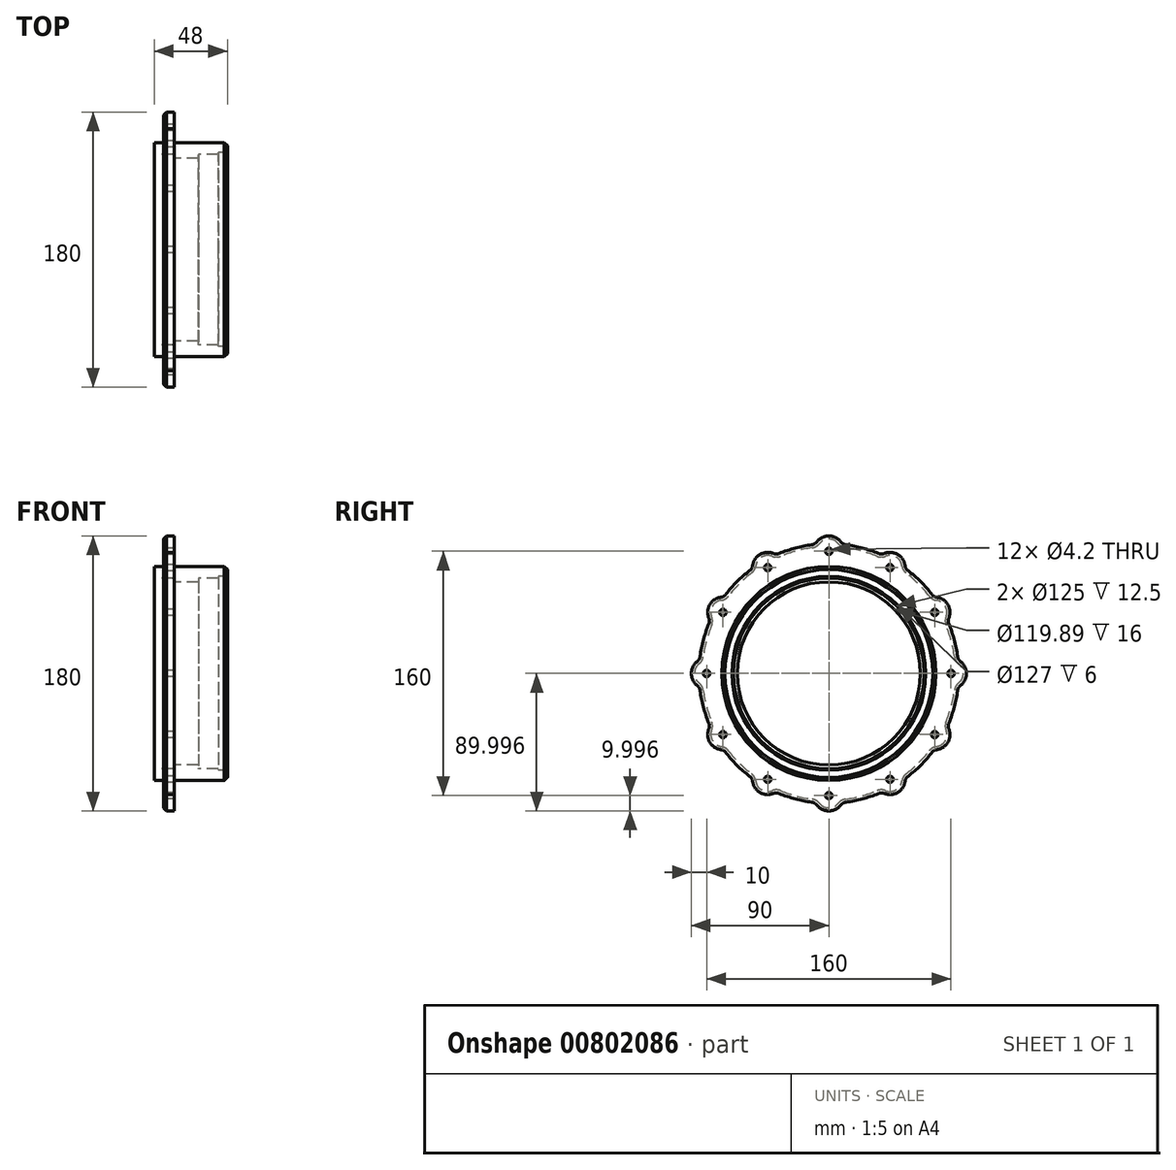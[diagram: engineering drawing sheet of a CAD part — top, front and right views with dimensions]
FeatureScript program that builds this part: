
annotation { "Feature Type Name" : "Feature", "Feature Type Description" : "" }
export const myFeature = defineFeature(function(context is Context, id is Id, definition is map)
    precondition{}
    {
        {
            var Q0;
            Q0=qCreatedBy(makeId("Front.planeOp"),FACE);
            var sketch = newSketch(context, id + "F0", { "sketchPlane" : qUnion([Q0])});
            skLineSegment(sketch, "E0", {"start": v(-16.87, 26.2) * mm, "end": v(-9.87, 26.2) * mm});
            skLineSegment(sketch, "E1", {"start": v(-9.87, 26.2) * mm, "end": v(-9.87, 6.2) * mm});
            skLineSegment(sketch, "E2", {"start": v(-16.87, 26.2) * mm, "end": v(-16.87, 6.2) * mm});
            skLineSegment(sketch, "E3", {"start": v(-16.87, 6.2) * mm, "end": v(-22.87, 6.2) * mm});
            skLineSegment(sketch, "E4", {"start": v(-22.87, 6.2) * mm, "end": v(-22.87, -1.3) * mm});
            skLineSegment(sketch, "E5", {"start": v(-22.87, -1.3) * mm, "end": v(-9.87, -1.3) * mm});
            skLineSegment(sketch, "E6", {"start": v(-9.87, -1.3) * mm, "end": v(-9.87, -3.85) * mm});
            skLineSegment(sketch, "E7", {"start": v(-9.87, -3.85) * mm, "end": v(6.13, -3.85) * mm});
            skLineSegment(sketch, "E8", {"start": v(6.13, -3.85) * mm, "end": v(6.13, -1.3) * mm});
            skLineSegment(sketch, "E9", {"start": v(6.13, -1.3) * mm, "end": v(19.13, -1.3) * mm});
            skLineSegment(sketch, "E10", {"start": v(-16.87, -63.8) * mm, "end": v(53.32, -63.8) * mm, "construction": true});
            skLineSegment(sketch, "E11", {"start": v(19.13, -1.3) * mm, "end": v(19.13, -0.3) * mm});
            skLineSegment(sketch, "E12", {"start": v(19.13, -0.3) * mm, "end": v(25.13, -0.3) * mm});
            skLineSegment(sketch, "E13", {"start": v(-9.87, 6.2) * mm, "end": v(25.13, 6.2) * mm});
            skLineSegment(sketch, "E14", {"start": v(25.13, 6.2) * mm, "end": v(25.13, -0.3) * mm});
            skSolve(sketch);
        }
        {
            var Q0;
            Q0 = qSketchRegion(id + "F0", true);
            var Q1;
            Q1=sQuery(id+"F0.wireOp",EDGE,"E10");
            revolve(context, id + "F1", {"entities" : qUnion([Q0]), "axis" : qUnion([Q1]), "revolveType" : RevolveType.FULL});
        }
        {
            var Q0;
            Q0=makeQuery(id+"F1.opRevolve","SWEPT_FACE",FACE,{"disambiguationData":[OSD([sQuery(id+"F0.wireOp",EDGE,"E2")])]});
            var sketch = newSketch(context, id + "F2", { "sketchPlane" : qUnion([Q0])});
            skLineSegment(sketch, "E15", {"start": v(0, -63.8) * mm, "end": v(0, 16.2) * mm, "construction": true});
            skPoint(sketch, "E16", {"position": v(0, 16.2) * mm});
            skPoint(sketch, "E17.1.0", {"position": v(-40, 5.49) * mm});
            skPoint(sketch, "E17.2.0", {"position": v(-69.28, -23.8) * mm});
            skPoint(sketch, "E17.3.0", {"position": v(-80, -63.8) * mm});
            skPoint(sketch, "E17.4.0", {"position": v(-69.28, -103.8) * mm});
            skPoint(sketch, "E17.5.0", {"position": v(-40, -133.08) * mm});
            skPoint(sketch, "E17.6.0", {"position": v(0, -143.8) * mm});
            skPoint(sketch, "E17.7.0", {"position": v(40, -133.08) * mm});
            skPoint(sketch, "E17.8.0", {"position": v(69.28, -103.8) * mm});
            skPoint(sketch, "E17.9.0", {"position": v(80, -63.8) * mm});
            skPoint(sketch, "E17.10.0", {"position": v(69.28, -23.8) * mm});
            skPoint(sketch, "E17.11.0", {"position": v(40, 5.49) * mm});
            skPoint(sketch, "E17.center", {"position": v(0, -63.8) * mm});
            skSolve(sketch);
        }
        {
            var Q0;
            Q0=sQuery(id+"F2.wireOp",VERTEX,"E16");
            var Q1;
            Q1=sQuery(id+"F2.wireOp",VERTEX,"E17.11.0");
            var Q2;
            Q2=sQuery(id+"F2.wireOp",VERTEX,"E17.10.0");
            var Q3;
            Q3=sQuery(id+"F2.wireOp",VERTEX,"E17.9.0");
            var Q4;
            Q4=sQuery(id+"F2.wireOp",VERTEX,"E17.8.0");
            var Q5;
            Q5=sQuery(id+"F2.wireOp",VERTEX,"E17.7.0");
            var Q6;
            Q6=sQuery(id+"F2.wireOp",VERTEX,"E17.6.0");
            var Q7;
            Q7=sQuery(id+"F2.wireOp",VERTEX,"E17.5.0");
            var Q8;
            Q8=sQuery(id+"F2.wireOp",VERTEX,"E17.4.0");
            var Q9;
            Q9=sQuery(id+"F2.wireOp",VERTEX,"E17.3.0");
            var Q10;
            Q10=sQuery(id+"F2.wireOp",VERTEX,"E17.2.0");
            var Q11;
            Q11=sQuery(id+"F2.wireOp",VERTEX,"E17.1.0");
            var Q12;
            Q12=makeQuery(id+"F1.opRevolve","SWEPT_BODY",BODY,{"disambiguationData":[OSD([sQuery(id+"F0.wireOp",EDGE,"E0"),sQuery(id+"F0.wireOp",EDGE,"E1"),sQuery(id+"F0.wireOp",EDGE,"E2"),sQuery(id+"F0.wireOp",EDGE,"E3"),sQuery(id+"F0.wireOp",EDGE,"E4"),sQuery(id+"F0.wireOp",EDGE,"E5"),sQuery(id+"F0.wireOp",EDGE,"E6"),sQuery(id+"F0.wireOp",EDGE,"E7"),sQuery(id+"F0.wireOp",EDGE,"E8"),sQuery(id+"F0.wireOp",EDGE,"E9"),sQuery(id+"F0.wireOp",EDGE,"E11"),sQuery(id+"F0.wireOp",EDGE,"E12"),sQuery(id+"F0.wireOp",EDGE,"E13"),sQuery(id+"F0.wireOp",EDGE,"E14")])]});
            hole(context, id + "F3", {"style" : HoleStyle.SIMPLE, "endStyle" : HoleEndStyle.THROUGH, "standardTappedOrClearance" : lookupTablePath({ "standard" : "ISO", "engagement" : "75%", "pitch" : "0.8 mm", "size" : "M5", "type" : "Tapped" }), "standardBlindInLast" : lookupTablePath({ "standard" : "ISO", "engagement" : "75%", "pitch" : "0.8 mm", "size" : "M5", "type" : "Tapped" }), "holeDiameter" : 4.2 * mm, "showTappedDepth" : true, "isTappedThrough" : true, "tappedDepth" : 16.82 * mm, "tapClearance" : 3, "startFromSketch" : true, "locations" : qUnion([Q0, Q1, Q2, Q3, Q4, Q5, Q6, Q7, Q8, Q9, Q10, Q11]), "scope" : qUnion([Q12]), "majorDiameter" : 5 * mm});
        }
        {
            var Q0;
            Q0=makeQuery(id+"F1.opRevolve","SWEPT_FACE",FACE,{"disambiguationData":[OSD([sQuery(id+"F0.wireOp",EDGE,"E1")])]});
            var sketch = newSketch(context, id + "F4", { "sketchPlane" : qUnion([Q0])});
            skArc(sketch, "E18", {"start": v(45, 14.15) * mm, "mid": v(40.7, 15.46) * mm, "end": v(36.24, 14.75) * mm});
            skArc(sketch, "E19", {"start": v(7.89, 22.35) * mm, "mid": v(4.39, 25.2) * mm, "end": v(0, 26.2) * mm});
            skArc(sketch, "E20", {"start": v(32.45, 14.77) * mm, "mid": v(22, 18.3) * mm, "end": v(11.18, 20.47) * mm});
            skLineSegment(sketch, "E21", {"start": v(0, -63.8) * mm, "end": v(0, 34.34) * mm, "construction": true});
            skLineSegment(sketch, "E22", {"start": v(0, -63.8) * mm, "end": v(49.04, 21.14) * mm, "construction": true});
            skPoint(sketch, "E23.visualSharp", {"position": v(8.91, 20.74) * mm});
            skArc(sketch, "E23.filletArc", {"start": v(7.89, 22.35) * mm, "mid": v(9.35, 21.09) * mm, "end": v(11.18, 20.47) * mm});
            skPoint(sketch, "E24.visualSharp", {"position": v(34.55, 13.87) * mm});
            skArc(sketch, "E24.filletArc", {"start": v(32.45, 14.77) * mm, "mid": v(34.35, 14.39) * mm, "end": v(36.24, 14.75) * mm});
            skPoint(sketch, "E25.1.0", {"position": v(-34.55, 13.87) * mm});
            skArc(sketch, "E25.1.1", {"start": v(-11.18, 20.47) * mm, "mid": v(-22, 18.3) * mm, "end": v(-32.45, 14.77) * mm});
            skArc(sketch, "E25.1.2", {"start": v(-36.24, 14.75) * mm, "mid": v(-40.7, 15.46) * mm, "end": v(-45, 14.15) * mm});
            skPoint(sketch, "E25.1.3", {"position": v(-8.91, 20.74) * mm});
            skArc(sketch, "E25.1.4", {"start": v(0, 26.2) * mm, "mid": v(-4.39, 25.2) * mm, "end": v(-7.89, 22.35) * mm});
            skArc(sketch, "E25.1.5", {"start": v(-11.18, 20.47) * mm, "mid": v(-9.35, 21.09) * mm, "end": v(-7.89, 22.35) * mm});
            skArc(sketch, "E25.1.6", {"start": v(-36.24, 14.75) * mm, "mid": v(-34.35, 14.39) * mm, "end": v(-32.45, 14.77) * mm});
            skPoint(sketch, "E25.2.0", {"position": v(-68.75, -13.8) * mm});
            skArc(sketch, "E25.2.1", {"start": v(-51.8, 3.6) * mm, "mid": v(-60.1, -3.7) * mm, "end": v(-67.39, -11.98) * mm});
            skArc(sketch, "E25.2.2", {"start": v(-70.66, -13.89) * mm, "mid": v(-74.87, -15.5) * mm, "end": v(-77.94, -18.8) * mm});
            skPoint(sketch, "E25.2.3", {"position": v(-49.99, 4.95) * mm});
            skArc(sketch, "E25.2.4", {"start": v(-45, 14.15) * mm, "mid": v(-48.3, 11.07) * mm, "end": v(-49.9, 6.87) * mm});
            skArc(sketch, "E25.2.5", {"start": v(-51.8, 3.6) * mm, "mid": v(-50.53, 5.04) * mm, "end": v(-49.9, 6.87) * mm});
            skArc(sketch, "E25.2.6", {"start": v(-70.66, -13.89) * mm, "mid": v(-68.84, -13.26) * mm, "end": v(-67.39, -11.98) * mm});
            skPoint(sketch, "E25.3.0", {"position": v(-84.53, -54.88) * mm});
            skArc(sketch, "E25.3.1", {"start": v(-78.56, -31.34) * mm, "mid": v(-82.1, -41.8) * mm, "end": v(-84.26, -52.62) * mm});
            skArc(sketch, "E25.3.2", {"start": v(-86.15, -55.9) * mm, "mid": v(-88.98, -59.4) * mm, "end": v(-90, -63.8) * mm});
            skPoint(sketch, "E25.3.3", {"position": v(-77.66, -29.25) * mm});
            skArc(sketch, "E25.3.4", {"start": v(-77.94, -18.8) * mm, "mid": v(-79.26, -23.1) * mm, "end": v(-78.55, -27.55) * mm});
            skArc(sketch, "E25.3.5", {"start": v(-78.56, -31.34) * mm, "mid": v(-78.18, -29.45) * mm, "end": v(-78.55, -27.55) * mm});
            skArc(sketch, "E25.3.6", {"start": v(-86.15, -55.9) * mm, "mid": v(-84.88, -54.45) * mm, "end": v(-84.26, -52.62) * mm});
            skPoint(sketch, "E25.4.0", {"position": v(-77.66, -98.34) * mm});
            skArc(sketch, "E25.4.1", {"start": v(-84.26, -74.97) * mm, "mid": v(-82.1, -85.8) * mm, "end": v(-78.56, -96.25) * mm});
            skArc(sketch, "E25.4.2", {"start": v(-78.55, -100.04) * mm, "mid": v(-79.26, -104.48) * mm, "end": v(-77.94, -108.8) * mm});
            skPoint(sketch, "E25.4.3", {"position": v(-84.53, -72.7) * mm});
            skArc(sketch, "E25.4.4", {"start": v(-90, -63.8) * mm, "mid": v(-88.98, -68.18) * mm, "end": v(-86.15, -71.68) * mm});
            skArc(sketch, "E25.4.5", {"start": v(-84.26, -74.97) * mm, "mid": v(-84.88, -73.14) * mm, "end": v(-86.15, -71.68) * mm});
            skArc(sketch, "E25.4.6", {"start": v(-78.55, -100.04) * mm, "mid": v(-78.18, -98.14) * mm, "end": v(-78.56, -96.25) * mm});
            skPoint(sketch, "E25.5.0", {"position": v(-49.99, -132.54) * mm});
            skArc(sketch, "E25.5.1", {"start": v(-67.39, -115.6) * mm, "mid": v(-60.1, -123.9) * mm, "end": v(-51.8, -131.18) * mm});
            skArc(sketch, "E25.5.2", {"start": v(-49.9, -134.45) * mm, "mid": v(-48.3, -138.66) * mm, "end": v(-45, -141.74) * mm});
            skPoint(sketch, "E25.5.3", {"position": v(-68.75, -113.78) * mm});
            skArc(sketch, "E25.5.4", {"start": v(-77.94, -108.8) * mm, "mid": v(-74.87, -112.09) * mm, "end": v(-70.66, -113.7) * mm});
            skArc(sketch, "E25.5.5", {"start": v(-67.39, -115.6) * mm, "mid": v(-68.84, -114.33) * mm, "end": v(-70.66, -113.7) * mm});
            skArc(sketch, "E25.5.6", {"start": v(-49.9, -134.45) * mm, "mid": v(-50.53, -132.63) * mm, "end": v(-51.8, -131.18) * mm});
            skPoint(sketch, "E25.6.0", {"position": v(-8.91, -148.33) * mm});
            skArc(sketch, "E25.6.1", {"start": v(-32.45, -142.36) * mm, "mid": v(-22, -145.9) * mm, "end": v(-11.18, -148.06) * mm});
            skArc(sketch, "E25.6.2", {"start": v(-7.89, -149.94) * mm, "mid": v(-4.39, -152.78) * mm, "end": v(0, -153.8) * mm});
            skPoint(sketch, "E25.6.3", {"position": v(-34.55, -141.46) * mm});
            skArc(sketch, "E25.6.4", {"start": v(-45, -141.74) * mm, "mid": v(-40.7, -143.05) * mm, "end": v(-36.24, -142.34) * mm});
            skArc(sketch, "E25.6.5", {"start": v(-32.45, -142.36) * mm, "mid": v(-34.35, -141.98) * mm, "end": v(-36.24, -142.34) * mm});
            skArc(sketch, "E25.6.6", {"start": v(-7.89, -149.94) * mm, "mid": v(-9.35, -148.67) * mm, "end": v(-11.18, -148.06) * mm});
            skPoint(sketch, "E25.7.0", {"position": v(34.55, -141.46) * mm});
            skArc(sketch, "E25.7.1", {"start": v(11.18, -148.06) * mm, "mid": v(22, -145.9) * mm, "end": v(32.45, -142.36) * mm});
            skArc(sketch, "E25.7.2", {"start": v(36.24, -142.34) * mm, "mid": v(40.7, -143.05) * mm, "end": v(45, -141.74) * mm});
            skPoint(sketch, "E25.7.3", {"position": v(8.91, -148.33) * mm});
            skArc(sketch, "E25.7.4", {"start": v(0, -153.8) * mm, "mid": v(4.39, -152.78) * mm, "end": v(7.89, -149.94) * mm});
            skArc(sketch, "E25.7.5", {"start": v(11.18, -148.06) * mm, "mid": v(9.35, -148.67) * mm, "end": v(7.89, -149.94) * mm});
            skArc(sketch, "E25.7.6", {"start": v(36.24, -142.34) * mm, "mid": v(34.35, -141.98) * mm, "end": v(32.45, -142.36) * mm});
            skPoint(sketch, "E25.8.0", {"position": v(68.75, -113.78) * mm});
            skArc(sketch, "E25.8.1", {"start": v(51.8, -131.18) * mm, "mid": v(60.1, -123.9) * mm, "end": v(67.39, -115.6) * mm});
            skArc(sketch, "E25.8.2", {"start": v(70.66, -113.7) * mm, "mid": v(74.87, -112.09) * mm, "end": v(77.94, -108.8) * mm});
            skPoint(sketch, "E25.8.3", {"position": v(49.99, -132.54) * mm});
            skArc(sketch, "E25.8.4", {"start": v(45, -141.74) * mm, "mid": v(48.3, -138.66) * mm, "end": v(49.9, -134.45) * mm});
            skArc(sketch, "E25.8.5", {"start": v(51.8, -131.18) * mm, "mid": v(50.53, -132.63) * mm, "end": v(49.9, -134.45) * mm});
            skArc(sketch, "E25.8.6", {"start": v(70.66, -113.7) * mm, "mid": v(68.84, -114.33) * mm, "end": v(67.39, -115.6) * mm});
            skPoint(sketch, "E25.9.0", {"position": v(84.53, -72.7) * mm});
            skArc(sketch, "E25.9.1", {"start": v(78.56, -96.25) * mm, "mid": v(82.1, -85.8) * mm, "end": v(84.26, -74.97) * mm});
            skArc(sketch, "E25.9.2", {"start": v(86.15, -71.68) * mm, "mid": v(88.98, -68.18) * mm, "end": v(90, -63.8) * mm});
            skPoint(sketch, "E25.9.3", {"position": v(77.66, -98.34) * mm});
            skArc(sketch, "E25.9.4", {"start": v(77.94, -108.8) * mm, "mid": v(79.26, -104.48) * mm, "end": v(78.55, -100.04) * mm});
            skArc(sketch, "E25.9.5", {"start": v(78.56, -96.25) * mm, "mid": v(78.18, -98.14) * mm, "end": v(78.55, -100.04) * mm});
            skArc(sketch, "E25.9.6", {"start": v(86.15, -71.68) * mm, "mid": v(84.88, -73.14) * mm, "end": v(84.26, -74.97) * mm});
            skPoint(sketch, "E25.10.0", {"position": v(77.66, -29.25) * mm});
            skArc(sketch, "E25.10.1", {"start": v(84.26, -52.62) * mm, "mid": v(82.1, -41.8) * mm, "end": v(78.56, -31.34) * mm});
            skArc(sketch, "E25.10.2", {"start": v(78.55, -27.55) * mm, "mid": v(79.26, -23.1) * mm, "end": v(77.94, -18.8) * mm});
            skPoint(sketch, "E25.10.3", {"position": v(84.53, -54.88) * mm});
            skArc(sketch, "E25.10.4", {"start": v(90, -63.8) * mm, "mid": v(88.98, -59.4) * mm, "end": v(86.15, -55.9) * mm});
            skArc(sketch, "E25.10.5", {"start": v(84.26, -52.62) * mm, "mid": v(84.88, -54.45) * mm, "end": v(86.15, -55.9) * mm});
            skArc(sketch, "E25.10.6", {"start": v(78.55, -27.55) * mm, "mid": v(78.18, -29.45) * mm, "end": v(78.56, -31.34) * mm});
            skPoint(sketch, "E25.11.0", {"position": v(49.99, 4.95) * mm});
            skArc(sketch, "E25.11.1", {"start": v(67.39, -11.98) * mm, "mid": v(60.1, -3.7) * mm, "end": v(51.8, 3.6) * mm});
            skArc(sketch, "E25.11.2", {"start": v(49.9, 6.87) * mm, "mid": v(48.3, 11.07) * mm, "end": v(45, 14.15) * mm});
            skPoint(sketch, "E25.11.3", {"position": v(68.75, -13.8) * mm});
            skArc(sketch, "E25.11.4", {"start": v(77.94, -18.8) * mm, "mid": v(74.87, -15.5) * mm, "end": v(70.66, -13.89) * mm});
            skArc(sketch, "E25.11.5", {"start": v(67.39, -11.98) * mm, "mid": v(68.84, -13.26) * mm, "end": v(70.66, -13.89) * mm});
            skArc(sketch, "E25.11.6", {"start": v(49.9, 6.87) * mm, "mid": v(50.53, 5.04) * mm, "end": v(51.8, 3.6) * mm});
            skCircle(sketch, "E26", {"center": v(0, -63.8) * mm, "radius": 105.65 * mm});
            skSolve(sketch);
        }
        {
            var Q0;
            Q0 = qSketchRegion(id + "F4", true);
            extrude(context, id + "F5", {"entities" : qUnion([Q0]), "operationType" : NewBodyOperationType.REMOVE, "endBound" : BoundingType.THROUGH_ALL, "oppositeDirection" : true, "depth" : 25 * mm, "offsetDistance" : 25 * mm});
        }
        {
            var Q0;
            Q0=makeQuery(id+"F1.opRevolve","SWEPT_EDGE",EDGE,{"disambiguationData":[OSD([sQuery(id+"F0.wireOp",EDGE,"E13"),sQuery(id+"F0.wireOp",EDGE,"E14")])]});
            var Q1;
            Q1=makeQuery(id+"F1.opRevolve","SWEPT_EDGE",EDGE,{"disambiguationData":[OSD([sQuery(id+"F0.wireOp",EDGE,"E0"),sQuery(id+"F0.wireOp",EDGE,"E2")])]});
            chamfer(context, id + "F6", {"entities" : qUnion([Q0, Q1]), "width" : 2 * mm, "tangentPropagation" : true});
        }
        {
            var Q0;
            Q0=makeQuery(id+"F5.boolean.opBoolean","INTERSECT",EDGE,{"derivedFrom":[makeQuery(id+"F1.opRevolve","SWEPT_FACE",FACE,{"disambiguationData":[OSD([sQuery(id+"F0.wireOp",EDGE,"E2")])]}),makeQuery(id+"F5.opExtrude","SWEPT_FACE",FACE,{"disambiguationData":[OSD([sQuery(id+"F4.wireOp",EDGE,"E20")])]})]});
            chamfer(context, id + "F7", {"entities" : qUnion([Q0]), "width" : 2 * mm, "tangentPropagation" : true});
        }
        {
            var Q0;
            Q0=makeQuery(id+"F1.opRevolve","SWEPT_EDGE",EDGE,{"disambiguationData":[OSD([sQuery(id+"F0.wireOp",EDGE,"E8"),sQuery(id+"F0.wireOp",EDGE,"E9")])]});
            fillet(context, id + "F8", {"entities" : qUnion([Q0]), "radius" : .5 * mm, "tangentPropagation" : true, "allowEdgeOverflow" : false});
        }
        {
            var Q0;
            Q0=makeQuery(id+"F1.opRevolve","SWEPT_EDGE",EDGE,{"disambiguationData":[OSD([sQuery(id+"F0.wireOp",EDGE,"E5"),sQuery(id+"F0.wireOp",EDGE,"E6")])]});
            fillet(context, id + "F9", {"entities" : qUnion([Q0]), "radius" : .5 * mm, "tangentPropagation" : true, "allowEdgeOverflow" : false});
        }
        {
            var Q0;
            Q0=makeQuery(id+"F1.opRevolve","SWEPT_EDGE",EDGE,{"disambiguationData":[OSD([sQuery(id+"F0.wireOp",EDGE,"E2"),sQuery(id+"F0.wireOp",EDGE,"E3")])]});
            var Q1;
            Q1=makeQuery(id+"F1.opRevolve","SWEPT_EDGE",EDGE,{"disambiguationData":[OSD([sQuery(id+"F0.wireOp",EDGE,"E1"),sQuery(id+"F0.wireOp",EDGE,"E13")])]});
            fillet(context, id + "F10", {"entities" : qUnion([Q0, Q1]), "radius" : .5 * mm, "tangentPropagation" : true, "allowEdgeOverflow" : false});
        }
    });
